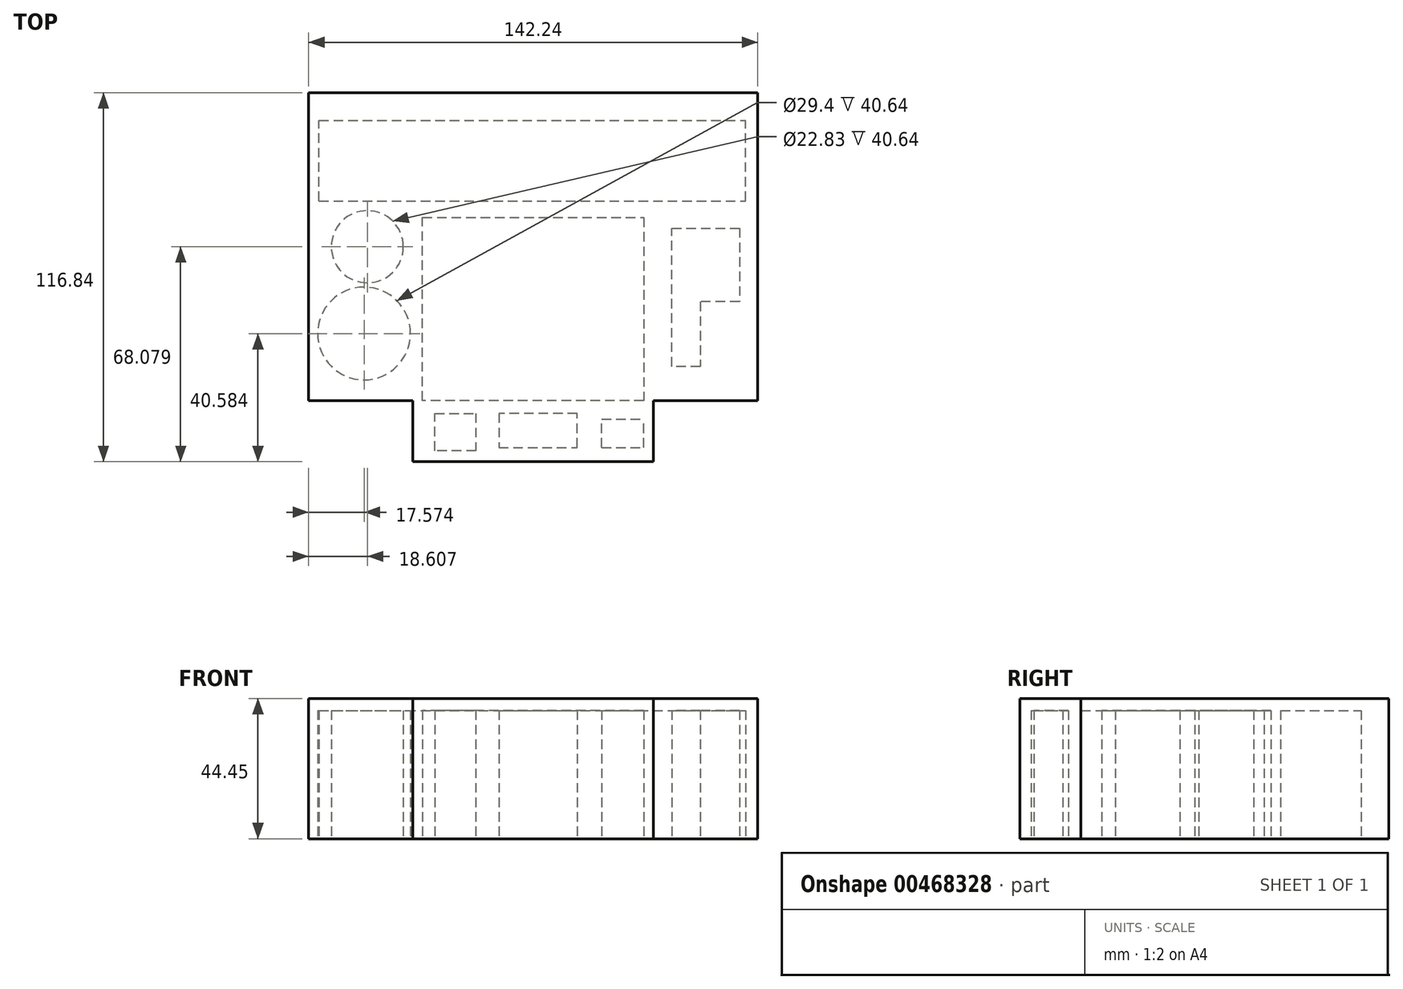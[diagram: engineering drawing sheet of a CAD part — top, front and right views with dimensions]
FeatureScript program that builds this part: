
annotation { "Feature Type Name" : "Feature", "Feature Type Description" : "" }
export const myFeature = defineFeature(function(context is Context, id is Id, definition is map)
    precondition{}
    {
        {
            var Q0;
            Q0=qCreatedBy(makeId("Top.planeOp"),FACE);
            var sketch = newSketch(context, id + "F0", { "sketchPlane" : qUnion([Q0])});
            skLineSegment(sketch, "E0", {"start": v(0, -19.32) * mm, "end": v(0, 64.5) * mm});
            skLineSegment(sketch, "E1", {"start": v(0, 64.5) * mm, "end": v(76.2, 64.5) * mm});
            skLineSegment(sketch, "E2", {"start": v(76.2, 64.5) * mm, "end": v(76.2, -19.32) * mm});
            skLineSegment(sketch, "E3", {"start": v(76.2, -19.32) * mm, "end": v(0, -19.32) * mm});
            skSolve(sketch);
        }
        {
            var Q0;
            Q0 = qSketchRegion(id + "F0", true);
            extrude(context, id + "F1", {"entities" : qUnion([Q0]), "depth" : 19.05 * mm});
        }
        {
            var Q0;
            Q0=makeQuery(id+"F1.opExtrude","CAP_FACE",FACE,{"disambiguationData":[OSD([sQuery(id+"F0.wireOp",EDGE,"E0"),sQuery(id+"F0.wireOp",EDGE,"E1"),sQuery(id+"F0.wireOp",EDGE,"E2"),sQuery(id+"F0.wireOp",EDGE,"E3")])],"isStart":true});
            var sketch = newSketch(context, id + "F2", { "sketchPlane" : qUnion([Q0])});
            skLineSegment(sketch, "E4", {"start": v(3.08, 0) * mm, "end": v(3.08, -58) * mm});
            skLineSegment(sketch, "E5", {"start": v(3.08, -58) * mm, "end": v(73.1, -58) * mm});
            skLineSegment(sketch, "E6", {"start": v(73.1, -58) * mm, "end": v(73.1, 0) * mm});
            skLineSegment(sketch, "E7", {"start": v(73.1, 0) * mm, "end": v(3.08, 0) * mm});
            skSolve(sketch);
        }
        {
            var Q0;
            Q0=makeQuery(id+"F2.imprint","IMPRINT",FACE,{"disambiguationData":[TD([[makeQuery(id+"F2.imprint","IMPRINT",EDGE,{"derivedFrom":sQuery(id+"F2.wireOp",EDGE,"E4")}),1.0]])]});
            extrude(context, id + "F3", {"entities" : qUnion([Q0]), "operationType" : NewBodyOperationType.REMOVE, "oppositeDirection" : true, "depth" : 15.24 * mm});
        }
        {
            var Q0;
            Q0=makeQuery(id+"F1.opExtrude","CAP_FACE",FACE,{"disambiguationData":[OSD([sQuery(id+"F0.wireOp",EDGE,"E0"),sQuery(id+"F0.wireOp",EDGE,"E1"),sQuery(id+"F0.wireOp",EDGE,"E2"),sQuery(id+"F0.wireOp",EDGE,"E3")])],"isStart":true});
            var sketch = newSketch(context, id + "F4", { "sketchPlane" : qUnion([Q0])});
            skLineSegment(sketch, "E8", {"start": v(6.96, 15.86) * mm, "end": v(6.96, 4.02) * mm});
            skLineSegment(sketch, "E9", {"start": v(6.96, 4.02) * mm, "end": v(19.96, 4.02) * mm});
            skLineSegment(sketch, "E10", {"start": v(19.96, 4.02) * mm, "end": v(19.96, 15.86) * mm});
            skLineSegment(sketch, "E11", {"start": v(19.96, 15.86) * mm, "end": v(6.96, 15.86) * mm});
            skSolve(sketch);
        }
        {
            var Q0;
            Q0=makeQuery(id+"F4.imprint","IMPRINT",FACE,{"disambiguationData":[TD([[makeQuery(id+"F4.imprint","IMPRINT",EDGE,{"derivedFrom":sQuery(id+"F4.wireOp",EDGE,"E8")}),1.0]])]});
            extrude(context, id + "F5", {"entities" : qUnion([Q0]), "operationType" : NewBodyOperationType.REMOVE, "oppositeDirection" : true, "depth" : 15.24 * mm});
        }
        {
            var Q0;
            Q0=makeQuery(id+"F1.opExtrude","CAP_FACE",FACE,{"disambiguationData":[OSD([sQuery(id+"F0.wireOp",EDGE,"E0"),sQuery(id+"F0.wireOp",EDGE,"E1"),sQuery(id+"F0.wireOp",EDGE,"E2"),sQuery(id+"F0.wireOp",EDGE,"E3")])],"isStart":true});
            var sketch = newSketch(context, id + "F6", { "sketchPlane" : qUnion([Q0])});
            skLineSegment(sketch, "E12", {"start": v(27.23, 14.86) * mm, "end": v(52.04, 14.86) * mm});
            skLineSegment(sketch, "E13", {"start": v(52.04, 14.86) * mm, "end": v(52.04, 4.02) * mm});
            skLineSegment(sketch, "E14", {"start": v(52.04, 4.02) * mm, "end": v(27.23, 4.02) * mm});
            skLineSegment(sketch, "E15", {"start": v(27.23, 4.02) * mm, "end": v(27.23, 14.86) * mm});
            skSolve(sketch);
        }
        {
            var Q0;
            Q0=makeQuery(id+"F6.imprint","IMPRINT",FACE,{"disambiguationData":[TD([[makeQuery(id+"F6.imprint","IMPRINT",EDGE,{"derivedFrom":sQuery(id+"F6.wireOp",EDGE,"E12")}),-1.0]])]});
            extrude(context, id + "F7", {"entities" : qUnion([Q0]), "operationType" : NewBodyOperationType.REMOVE, "oppositeDirection" : true, "depth" : 15.24 * mm});
        }
        {
            var Q0;
            Q0=makeQuery(id+"F1.opExtrude","CAP_FACE",FACE,{"disambiguationData":[OSD([sQuery(id+"F0.wireOp",EDGE,"E0"),sQuery(id+"F0.wireOp",EDGE,"E1"),sQuery(id+"F0.wireOp",EDGE,"E2"),sQuery(id+"F0.wireOp",EDGE,"E3")])],"isStart":true});
            var sketch = newSketch(context, id + "F8", { "sketchPlane" : qUnion([Q0])});
            skLineSegment(sketch, "E16", {"start": v(59.8, 14.86) * mm, "end": v(59.8, 5.82) * mm});
            skLineSegment(sketch, "E17", {"start": v(59.8, 5.82) * mm, "end": v(73.1, 5.82) * mm});
            skLineSegment(sketch, "E18", {"start": v(59.8, 14.86) * mm, "end": v(73.1, 14.86) * mm});
            skLineSegment(sketch, "E19", {"start": v(73.1, 14.86) * mm, "end": v(73.1, 5.82) * mm});
            skLineSegment(sketch, "E20", {"start": v(73.1, 5.82) * mm, "end": v(73.1, 14.86) * mm});
            skSolve(sketch);
        }
        {
            var Q0;
            Q0=makeQuery(id+"F8.imprint","IMPRINT",FACE,{"disambiguationData":[TD([[makeQuery(id+"F8.imprint","IMPRINT",EDGE,{"derivedFrom":sQuery(id+"F8.wireOp",EDGE,"E16")}),1.0]])]});
            extrude(context, id + "F9", {"entities" : qUnion([Q0]), "operationType" : NewBodyOperationType.REMOVE, "oppositeDirection" : true, "depth" : 15.24 * mm});
        }
        {
            var Q0;
            Q0=makeQuery(id+"F1.opExtrude","SWEPT_FACE",FACE,{"disambiguationData":[OSD([sQuery(id+"F0.wireOp",EDGE,"E2")])]});
            var sketch = newSketch(context, id + "F10", { "sketchPlane" : qUnion([Q0])});
            skLineSegment(sketch, "E21", {"start": v(0, 0) * mm, "end": v(0, 19.05) * mm});
            skLineSegment(sketch, "E22", {"start": v(0, 19.05) * mm, "end": v(64.5, 19.05) * mm});
            skLineSegment(sketch, "E23", {"start": v(64.5, 19.05) * mm, "end": v(64.5, 0) * mm});
            skLineSegment(sketch, "E24", {"start": v(64.5, 0) * mm, "end": v(0, 0) * mm});
            skSolve(sketch);
        }
        {
            var Q0;
            Q0=makeQuery(id+"F10.imprint","IMPRINT",FACE,{"disambiguationData":[TD([[makeQuery(id+"F10.imprint","IMPRINT",EDGE,{"derivedFrom":sQuery(id+"F10.wireOp",EDGE,"E21")}),-1.0]])]});
            extrude(context, id + "F11", {"entities" : qUnion([Q0]), "operationType" : NewBodyOperationType.ADD, "depth" : 33.02 * mm});
        }
        {
            var Q0;
            Q0=makeQuery(id+"F1.opExtrude","SWEPT_FACE",FACE,{"disambiguationData":[OSD([sQuery(id+"F0.wireOp",EDGE,"E0")])]});
            var sketch = newSketch(context, id + "F12", { "sketchPlane" : qUnion([Q0])});
            skLineSegment(sketch, "E25", {"start": v(0, 0) * mm, "end": v(0, 19.05) * mm});
            skLineSegment(sketch, "E26", {"start": v(0, 19.05) * mm, "end": v(-64.5, 19.05) * mm});
            skLineSegment(sketch, "E27", {"start": v(-64.5, 19.05) * mm, "end": v(-64.5, 0) * mm});
            skLineSegment(sketch, "E28", {"start": v(-64.5, 0) * mm, "end": v(0, 0) * mm});
            skSolve(sketch);
        }
        {
            var Q0;
            Q0=makeQuery(id+"F12.imprint","IMPRINT",FACE,{"disambiguationData":[TD([[makeQuery(id+"F12.imprint","IMPRINT",EDGE,{"derivedFrom":sQuery(id+"F12.wireOp",EDGE,"E25")}),1.0]])]});
            extrude(context, id + "F13", {"entities" : qUnion([Q0]), "operationType" : NewBodyOperationType.ADD, "depth" : 33.02 * mm});
        }
        {
            var Q0;
            Q0=makeQuery(id+"F13.boolean.opBoolean","MERGE",FACE,{"derivedFrom":[makeQuery(id+"F11.boolean.opBoolean","MERGE",FACE,{"derivedFrom":[makeQuery(id+"F1.opExtrude","SWEPT_FACE",FACE,{"disambiguationData":[OSD([sQuery(id+"F0.wireOp",EDGE,"E1")])]}),makeQuery(id+"F11.opExtrude","SWEPT_FACE",FACE,{"disambiguationData":[OSD([sQuery(id+"F10.wireOp",EDGE,"E23")])]})]}),makeQuery(id+"F13.opExtrude","SWEPT_FACE",FACE,{"disambiguationData":[OSD([sQuery(id+"F12.wireOp",EDGE,"E27")])]})]});
            var sketch = newSketch(context, id + "F14", { "sketchPlane" : qUnion([Q0])});
            skLineSegment(sketch, "E29", {"start": v(33.02, 0) * mm, "end": v(33.02, 19.05) * mm});
            skLineSegment(sketch, "E30", {"start": v(33.02, 19.05) * mm, "end": v(-109.22, 19.05) * mm});
            skLineSegment(sketch, "E31", {"start": v(-109.22, 19.05) * mm, "end": v(-109.22, 0) * mm});
            skLineSegment(sketch, "E32", {"start": v(-109.22, 0) * mm, "end": v(33.02, 0) * mm});
            skSolve(sketch);
        }
        {
            var Q0;
            Q0=makeQuery(id+"F14.imprint","IMPRINT",FACE,{"disambiguationData":[TD([[makeQuery(id+"F14.imprint","IMPRINT",EDGE,{"derivedFrom":sQuery(id+"F14.wireOp",EDGE,"E29")}),-1.0]])]});
            extrude(context, id + "F15", {"entities" : qUnion([Q0]), "operationType" : NewBodyOperationType.ADD, "depth" : 33.02 * mm});
        }
        {
            var Q0;
            Q0=makeQuery(id+"F15.boolean.opBoolean","MERGE",FACE,{"derivedFrom":[makeQuery(id+"F13.boolean.opBoolean","MERGE",FACE,{"derivedFrom":[makeQuery(id+"F11.boolean.opBoolean","MERGE",FACE,{"derivedFrom":[makeQuery(id+"F1.opExtrude","CAP_FACE",FACE,{"disambiguationData":[OSD([sQuery(id+"F0.wireOp",EDGE,"E0"),sQuery(id+"F0.wireOp",EDGE,"E1"),sQuery(id+"F0.wireOp",EDGE,"E2"),sQuery(id+"F0.wireOp",EDGE,"E3")])],"isStart":true}),makeQuery(id+"F11.opExtrude","SWEPT_FACE",FACE,{"disambiguationData":[OSD([sQuery(id+"F10.wireOp",EDGE,"E24")])]})]}),makeQuery(id+"F13.opExtrude","SWEPT_FACE",FACE,{"disambiguationData":[OSD([sQuery(id+"F12.wireOp",EDGE,"E28")])]})]}),makeQuery(id+"F15.opExtrude","SWEPT_FACE",FACE,{"disambiguationData":[OSD([sQuery(id+"F14.wireOp",EDGE,"E32")])]})]});
            var sketch = newSketch(context, id + "F16", { "sketchPlane" : qUnion([Q0])});
            skLineSegment(sketch, "E33.bottom", {"start": v(-29.68, -63.25) * mm, "end": v(105.42, -63.25) * mm});
            skLineSegment(sketch, "E33.top", {"start": v(-29.68, -88.72) * mm, "end": v(105.42, -88.72) * mm});
            skLineSegment(sketch, "E33.left", {"start": v(-29.68, -63.25) * mm, "end": v(-29.68, -88.72) * mm});
            skLineSegment(sketch, "E33.right", {"start": v(105.42, -63.25) * mm, "end": v(105.42, -88.72) * mm});
            skSolve(sketch);
        }
        {
            var Q0;
            Q0=makeQuery(id+"F16.imprint","IMPRINT",FACE,{"disambiguationData":[TD([[makeQuery(id+"F16.imprint","IMPRINT",EDGE,{"derivedFrom":sQuery(id+"F16.wireOp",EDGE,"E33.bottom")}),-1.0]])]});
            extrude(context, id + "F17", {"entities" : qUnion([Q0]), "operationType" : NewBodyOperationType.REMOVE, "oppositeDirection" : true, "depth" : 15.24 * mm});
        }
        {
            var Q0;
            Q0=makeQuery(id+"F15.boolean.opBoolean","MERGE",FACE,{"derivedFrom":[makeQuery(id+"F13.boolean.opBoolean","MERGE",FACE,{"derivedFrom":[makeQuery(id+"F11.boolean.opBoolean","MERGE",FACE,{"derivedFrom":[makeQuery(id+"F1.opExtrude","CAP_FACE",FACE,{"disambiguationData":[OSD([sQuery(id+"F0.wireOp",EDGE,"E0"),sQuery(id+"F0.wireOp",EDGE,"E1"),sQuery(id+"F0.wireOp",EDGE,"E2"),sQuery(id+"F0.wireOp",EDGE,"E3")])],"isStart":true}),makeQuery(id+"F11.opExtrude","SWEPT_FACE",FACE,{"disambiguationData":[OSD([sQuery(id+"F10.wireOp",EDGE,"E24")])]})]}),makeQuery(id+"F13.opExtrude","SWEPT_FACE",FACE,{"disambiguationData":[OSD([sQuery(id+"F12.wireOp",EDGE,"E28")])]})]}),makeQuery(id+"F15.opExtrude","SWEPT_FACE",FACE,{"disambiguationData":[OSD([sQuery(id+"F14.wireOp",EDGE,"E32")])]})]});
            var sketch = newSketch(context, id + "F18", { "sketchPlane" : qUnion([Q0])});
            skCircle(sketch, "E34", {"center": v(-15.45, -21.26) * mm, "radius": 14.7 * mm});
            skSolve(sketch);
        }
        {
            var Q0;
            Q0=makeQuery(id+"F18.imprint","IMPRINT",FACE,{"disambiguationData":[TD([[makeQuery(id+"F18.imprint","IMPRINT",EDGE,{"derivedFrom":sQuery(id+"F18.wireOp",EDGE,"E34")}),1.0]])]});
            var Q1;
            Q1=sQuery(id+"F18.wireOp",EDGE,"E34");
            extrude(context, id + "F19", {"entities" : qUnion([Q0]), "operationType" : NewBodyOperationType.REMOVE, "surfaceEntities" : qUnion([Q1]), "oppositeDirection" : true, "depth" : 15.24 * mm});
        }
        {
            var Q0;
            Q0=makeQuery(id+"F15.boolean.opBoolean","MERGE",FACE,{"derivedFrom":[makeQuery(id+"F13.boolean.opBoolean","MERGE",FACE,{"derivedFrom":[makeQuery(id+"F11.boolean.opBoolean","MERGE",FACE,{"derivedFrom":[makeQuery(id+"F1.opExtrude","CAP_FACE",FACE,{"disambiguationData":[OSD([sQuery(id+"F0.wireOp",EDGE,"E0"),sQuery(id+"F0.wireOp",EDGE,"E1"),sQuery(id+"F0.wireOp",EDGE,"E2"),sQuery(id+"F0.wireOp",EDGE,"E3")])],"isStart":true}),makeQuery(id+"F11.opExtrude","SWEPT_FACE",FACE,{"disambiguationData":[OSD([sQuery(id+"F10.wireOp",EDGE,"E24")])]})]}),makeQuery(id+"F13.opExtrude","SWEPT_FACE",FACE,{"disambiguationData":[OSD([sQuery(id+"F12.wireOp",EDGE,"E28")])]})]}),makeQuery(id+"F15.opExtrude","SWEPT_FACE",FACE,{"disambiguationData":[OSD([sQuery(id+"F14.wireOp",EDGE,"E32")])]})]});
            var sketch = newSketch(context, id + "F20", { "sketchPlane" : qUnion([Q0])});
            skCircle(sketch, "E35", {"center": v(-14.41, -48.76) * mm, "radius": 11.42 * mm});
            skPoint(sketch, "E35.centerSnap0", {"position": v(-33.02, -48.76) * mm});
            skSolve(sketch);
        }
        {
            var Q0;
            Q0=makeQuery(id+"F20.imprint","IMPRINT",FACE,{"disambiguationData":[TD([[makeQuery(id+"F20.imprint","IMPRINT",EDGE,{"derivedFrom":sQuery(id+"F20.wireOp",EDGE,"E35")}),1.0]])]});
            extrude(context, id + "F21", {"entities" : qUnion([Q0]), "operationType" : NewBodyOperationType.REMOVE, "oppositeDirection" : true, "depth" : 15.24 * mm});
        }
        {
            var Q0;
            Q0=makeQuery(id+"F15.boolean.opBoolean","MERGE",FACE,{"derivedFrom":[makeQuery(id+"F13.boolean.opBoolean","MERGE",FACE,{"derivedFrom":[makeQuery(id+"F11.boolean.opBoolean","MERGE",FACE,{"derivedFrom":[makeQuery(id+"F1.opExtrude","CAP_FACE",FACE,{"disambiguationData":[OSD([sQuery(id+"F0.wireOp",EDGE,"E0"),sQuery(id+"F0.wireOp",EDGE,"E1"),sQuery(id+"F0.wireOp",EDGE,"E2"),sQuery(id+"F0.wireOp",EDGE,"E3")])],"isStart":true}),makeQuery(id+"F11.opExtrude","SWEPT_FACE",FACE,{"disambiguationData":[OSD([sQuery(id+"F10.wireOp",EDGE,"E24")])]})]}),makeQuery(id+"F13.opExtrude","SWEPT_FACE",FACE,{"disambiguationData":[OSD([sQuery(id+"F12.wireOp",EDGE,"E28")])]})]}),makeQuery(id+"F15.opExtrude","SWEPT_FACE",FACE,{"disambiguationData":[OSD([sQuery(id+"F14.wireOp",EDGE,"E32")])]})]});
            var sketch = newSketch(context, id + "F22", { "sketchPlane" : qUnion([Q0])});
            skLineSegment(sketch, "E36", {"start": v(82.06, -10.82) * mm, "end": v(82.06, -54.63) * mm});
            skLineSegment(sketch, "E37", {"start": v(82.06, -54.63) * mm, "end": v(103.47, -54.63) * mm});
            skLineSegment(sketch, "E38", {"start": v(103.47, -54.63) * mm, "end": v(103.47, -31.3) * mm});
            skLineSegment(sketch, "E39", {"start": v(103.47, -31.3) * mm, "end": v(91.02, -31.3) * mm});
            skLineSegment(sketch, "E40", {"start": v(91.02, -31.3) * mm, "end": v(91.02, -10.82) * mm});
            skLineSegment(sketch, "E41", {"start": v(91.02, -10.82) * mm, "end": v(82.06, -10.82) * mm});
            skLineSegment(sketch, "E42", {"start": v(96.41, -9.14) * mm, "end": v(96.41, -26.35) * mm});
            skLineSegment(sketch, "E43", {"start": v(96.41, -26.35) * mm, "end": v(106, -26.35) * mm});
            skLineSegment(sketch, "E44", {"start": v(106, -26.35) * mm, "end": v(106, -9.14) * mm});
            skLineSegment(sketch, "E45", {"start": v(106, -9.14) * mm, "end": v(96.41, -9.14) * mm});
            skSolve(sketch);
        }
        {
            var Q0;
            Q0=makeQuery(id+"F22.imprint","IMPRINT",FACE,{"disambiguationData":[TD([[makeQuery(id+"F22.imprint","IMPRINT",EDGE,{"derivedFrom":sQuery(id+"F22.wireOp",EDGE,"E36")}),1.0]])]});
            extrude(context, id + "F23", {"entities" : qUnion([Q0]), "operationType" : NewBodyOperationType.REMOVE, "oppositeDirection" : true, "depth" : 15.24 * mm});
        }
        {
            var Q0;
            Q0=makeQuery(id+"F15.boolean.opBoolean","MERGE",FACE,{"derivedFrom":[makeQuery(id+"F13.boolean.opBoolean","MERGE",FACE,{"derivedFrom":[makeQuery(id+"F11.boolean.opBoolean","MERGE",FACE,{"derivedFrom":[makeQuery(id+"F1.opExtrude","CAP_FACE",FACE,{"disambiguationData":[OSD([sQuery(id+"F0.wireOp",EDGE,"E0"),sQuery(id+"F0.wireOp",EDGE,"E1"),sQuery(id+"F0.wireOp",EDGE,"E2"),sQuery(id+"F0.wireOp",EDGE,"E3")])],"isStart":true}),makeQuery(id+"F11.opExtrude","SWEPT_FACE",FACE,{"disambiguationData":[OSD([sQuery(id+"F10.wireOp",EDGE,"E24")])]})]}),makeQuery(id+"F13.opExtrude","SWEPT_FACE",FACE,{"disambiguationData":[OSD([sQuery(id+"F12.wireOp",EDGE,"E28")])]})]}),makeQuery(id+"F15.opExtrude","SWEPT_FACE",FACE,{"disambiguationData":[OSD([sQuery(id+"F14.wireOp",EDGE,"E32")])]})]});
            extrude(context, id + "F24", {"entities" : qUnion([Q0]), "operationType" : NewBodyOperationType.ADD, "depth" : 25.4 * mm, "offsetDistance" : 25.4 * mm});
        }
    });
